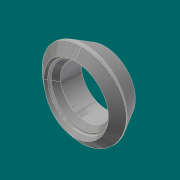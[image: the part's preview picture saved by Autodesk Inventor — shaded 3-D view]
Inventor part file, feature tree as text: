
AUTODESK INVENTOR PART (.ipt)
format: ipt  version: 2017.3 (Build 213257000, 257)  size: 424,960 bytes
history: native  units: mm (DEFAULTED — no unit token found)
features: other x7, sketch x5, plane x3, extrude x2, sweep x1, fillet x1
ambient origin geometry x8: Origin, YZ Plane, XZ Plane, XY Plane, X Axis, Y Axis, Z Axis, Center Point
bodies: Solid1 (feature_tree)
feature tree (19):
  sketch  "Sketch1"  dims[d5=44.45mm d8=90.0deg]
  plane  "Work Plane1"
  sketch  "Sketch2"  dims[d9=0.0mm d10=917.575mm]
  extrude  "Extrusion1"  TaperAngle=90.0deg  [1 undecoded]
  plane  "Work Plane2"
  sweep  "Sweep1"
  other  "Work Axis1"
  other  "Work Point1"
  other  "Work Point2"
  other  "Work Point3"
  plane  "Work Plane8"
  extrude  "Extrusion2"  [1 undecoded]
  fillet  "Fillet1"  Radius=73.66mm
  sketch  "Sketch3"  dims[d11=10.0mm d12=0.0mm d13=-503.2375mm d21=73.66mm]
  sketch  "3D Sketch1"
  other  "Edges3"
  other  "Edges4"
  other  "Work Axis2"
  sketch  "Sketch11"  dims[d22=6.0mm d23=4.0mm d24=2.0mm d25=90.0deg d26=30.1625mm d27=0.0mm d41=30.0deg d45=2.44475mm d50=39.37mm d51=44.45mm d52=122.2375mm d53=120.0deg d54=1191.41875mm d76=503.2375mm d77=0.0mm d79=2.19456mm d82=14.2875mm d83=8.290314mm d84=2.19456mm d85=0.0mm d86=0.0mm d87=90.0deg d88=0.0mm d89=90.0deg d90=93.6625mm d91=93.6625mm d92=0.0mm d93=-38.1mm d94=88.9mm d95=0.0mm d96=0.0mm d97=0.79375mm]
note: 2 required parameter values undecoded (feature->parameter linkage not recoverable at this tier; creation-order binding heuristic only, values carry confidence <= 0.55)
